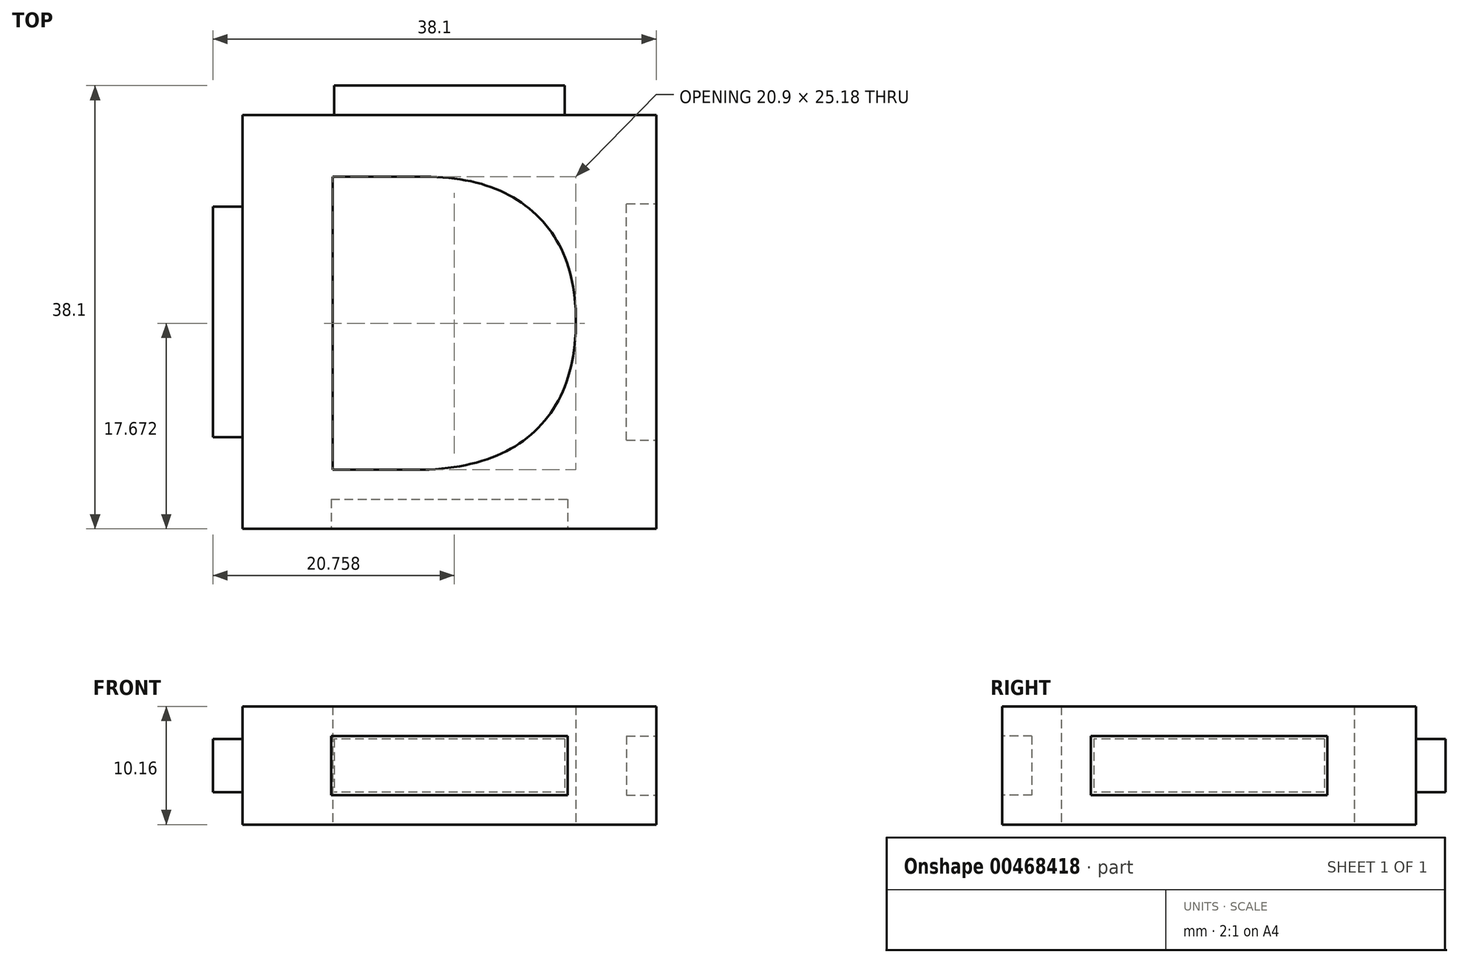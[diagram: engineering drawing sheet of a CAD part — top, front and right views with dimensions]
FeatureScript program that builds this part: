
annotation { "Feature Type Name" : "Feature", "Feature Type Description" : "" }
export const myFeature = defineFeature(function(context is Context, id is Id, definition is map)
    precondition{}
    {
        {
            var Q0;
            Q0=qCreatedBy(makeId("Top.planeOp"),FACE);
            var sketch = newSketch(context, id + "F0", { "sketchPlane" : qUnion([Q0])});
            skLineSegment(sketch, "E0.bottom", {"start": v(-17.78, 17.78) * mm, "end": v(17.78, 17.78) * mm});
            skLineSegment(sketch, "E0.top", {"start": v(-17.78, -17.78) * mm, "end": v(17.78, -17.78) * mm});
            skLineSegment(sketch, "E0.left", {"start": v(-17.78, 17.78) * mm, "end": v(-17.78, -17.78) * mm});
            skLineSegment(sketch, "E0.right", {"start": v(17.78, 17.78) * mm, "end": v(17.78, -17.78) * mm});
            skText(sketch, "E1", { "text": "D", "fontName": "OpenSans-Bold.ttf"});
            const initialGuessF0  = {"E1": [-0.01318, -0.0127, 1, 0, 0.0254]};
            skSetInitialGuess(sketch, initialGuessF0);
            skSolve(sketch);
        }
        {
            var Q0;
            Q0=qSketchRegion(id+"F0",true);
            extrude(context, id + "F1", {"entities" : qUnion([Q0]), "endBound" : BoundingType.SYMMETRIC, "depth" : 10.16 * mm});
        }
        {
            var Q0;
            Q0=makeQuery(id+"F1.opExtrude","SWEPT_FACE",FACE,{"disambiguationData":[OSD([sQuery(id+"F0.wireOp",EDGE,"E0.bottom")])]});
            var sketch = newSketch(context, id + "F2", { "sketchPlane" : qUnion([Q0])});
            skLineSegment(sketch, "E2.bottom", {"start": v(-9.9, 2.29) * mm, "end": v(9.9, 2.29) * mm});
            skLineSegment(sketch, "E2.top", {"start": v(-9.9, -2.29) * mm, "end": v(9.9, -2.29) * mm});
            skLineSegment(sketch, "E2.left", {"start": v(-9.9, 2.29) * mm, "end": v(-9.9, -2.29) * mm});
            skLineSegment(sketch, "E2.right", {"start": v(9.9, 2.29) * mm, "end": v(9.9, -2.29) * mm});
            skSolve(sketch);
        }
        {
            var Q0;
            Q0=qSketchRegion(id+"F2",true);
            extrude(context, id + "F3", {"entities" : qUnion([Q0]), "operationType" : NewBodyOperationType.ADD, "depth" : 2.54 * mm});
        }
        {
            var Q0;
            Q0=makeQuery(id+"F1.opExtrude","SWEPT_FACE",FACE,{"disambiguationData":[OSD([sQuery(id+"F0.wireOp",EDGE,"E0.left")])]});
            var sketch = newSketch(context, id + "F4", { "sketchPlane" : qUnion([Q0])});
            skLineSegment(sketch, "E3.bottom", {"start": v(-9.9, 2.29) * mm, "end": v(9.9, 2.29) * mm});
            skLineSegment(sketch, "E3.top", {"start": v(-9.9, -2.29) * mm, "end": v(9.9, -2.29) * mm});
            skLineSegment(sketch, "E3.left", {"start": v(-9.9, 2.29) * mm, "end": v(-9.9, -2.29) * mm});
            skLineSegment(sketch, "E3.right", {"start": v(9.9, 2.29) * mm, "end": v(9.9, -2.29) * mm});
            skSolve(sketch);
        }
        {
            var Q0;
            Q0=qSketchRegion(id+"F4",true);
            extrude(context, id + "F5", {"entities" : qUnion([Q0]), "operationType" : NewBodyOperationType.ADD, "depth" : 2.54 * mm});
        }
        {
            var Q0;
            Q0=makeQuery(id+"F1.opExtrude","SWEPT_FACE",FACE,{"disambiguationData":[OSD([sQuery(id+"F0.wireOp",EDGE,"E0.top")])]});
            var sketch = newSketch(context, id + "F6", { "sketchPlane" : qUnion([Q0])});
            skLineSegment(sketch, "E4.bottom", {"start": v(-10.16, 2.54) * mm, "end": v(10.16, 2.54) * mm});
            skLineSegment(sketch, "E4.top", {"start": v(-10.16, -2.54) * mm, "end": v(10.16, -2.54) * mm});
            skLineSegment(sketch, "E4.left", {"start": v(-10.16, 2.54) * mm, "end": v(-10.16, -2.54) * mm});
            skLineSegment(sketch, "E4.right", {"start": v(10.16, 2.54) * mm, "end": v(10.16, -2.54) * mm});
            skSolve(sketch);
        }
        {
            var Q0;
            Q0=qSketchRegion(id+"F6",true);
            extrude(context, id + "F7", {"entities" : qUnion([Q0]), "operationType" : NewBodyOperationType.REMOVE, "oppositeDirection" : true, "depth" : 2.54 * mm});
        }
        {
            var Q0;
            Q0=makeQuery(id+"F1.opExtrude","SWEPT_FACE",FACE,{"disambiguationData":[OSD([sQuery(id+"F0.wireOp",EDGE,"E0.right")])]});
            var sketch = newSketch(context, id + "F8", { "sketchPlane" : qUnion([Q0])});
            skLineSegment(sketch, "E5.bottom", {"start": v(-10.16, 2.54) * mm, "end": v(10.16, 2.54) * mm});
            skLineSegment(sketch, "E5.top", {"start": v(-10.16, -2.54) * mm, "end": v(10.16, -2.54) * mm});
            skLineSegment(sketch, "E5.left", {"start": v(-10.16, 2.54) * mm, "end": v(-10.16, -2.54) * mm});
            skLineSegment(sketch, "E5.right", {"start": v(10.16, 2.54) * mm, "end": v(10.16, -2.54) * mm});
            skSolve(sketch);
        }
        {
            var Q0;
            Q0=qSketchRegion(id+"F8",true);
            extrude(context, id + "F9", {"entities" : qUnion([Q0]), "operationType" : NewBodyOperationType.REMOVE, "oppositeDirection" : true, "depth" : 2.54 * mm});
        }
    });
